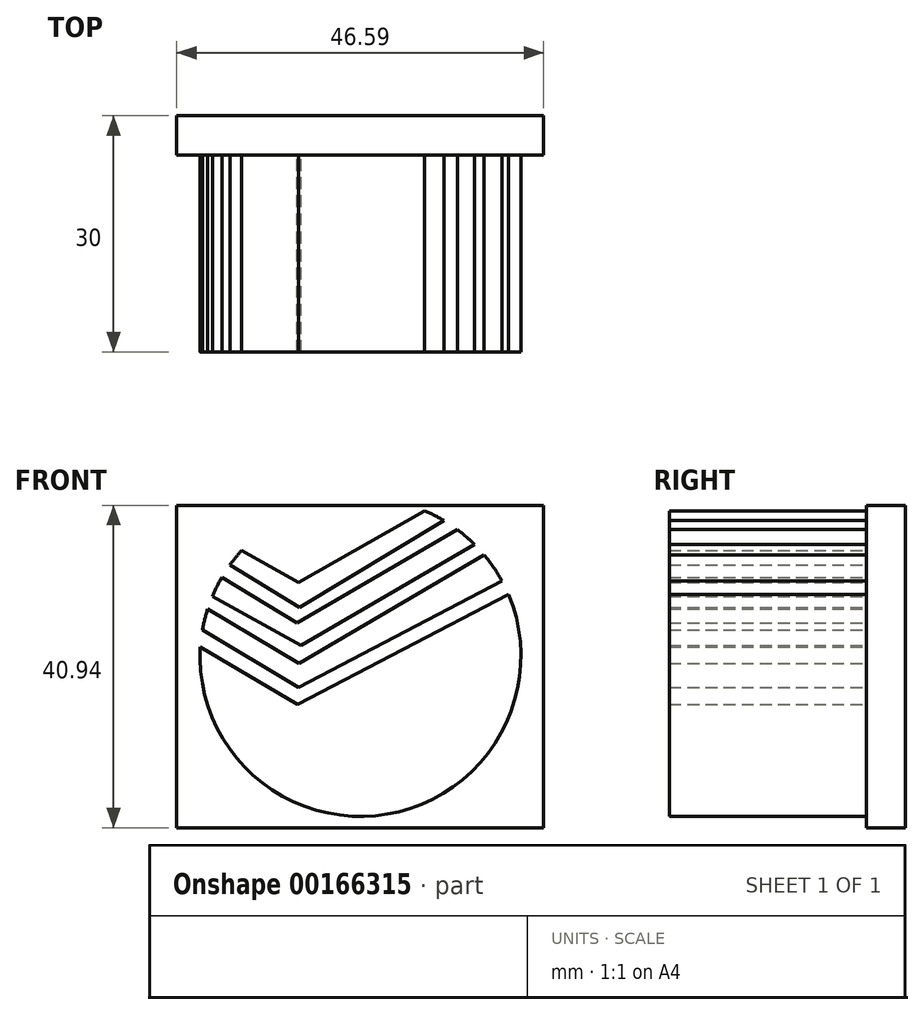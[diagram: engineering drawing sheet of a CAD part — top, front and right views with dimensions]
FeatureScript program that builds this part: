
annotation { "Feature Type Name" : "Feature", "Feature Type Description" : "" }
export const myFeature = defineFeature(function(context is Context, id is Id, definition is map)
    precondition{}
    {
        {
            var Q0;
            Q0=qCreatedBy(makeId("Front.planeOp"),FACE);
            var sketch = newSketch(context, id + "F0", { "sketchPlane" : qUnion([Q0])});
            skLineSegment(sketch, "E0", {"start": v(-23.24, 10.14) * mm, "end": v(-16.04, 6.02) * mm});
            skLineSegment(sketch, "E1", {"start": v(-16.04, 6.02) * mm, "end": v(0, 15.16) * mm});
            skLineSegment(sketch, "E2", {"start": v(-24.76, 8.25) * mm, "end": v(-15.88, 2.88) * mm});
            skLineSegment(sketch, "E3", {"start": v(-15.88, 2.88) * mm, "end": v(2.45, 13.9) * mm});
            skLineSegment(sketch, "E4", {"start": v(-25.77, 6.69) * mm, "end": v(-16.2, 0.9) * mm});
            skLineSegment(sketch, "E5", {"start": v(-16.2, 0.9) * mm, "end": v(4.16, 12.75) * mm});
            skLineSegment(sketch, "E6", {"start": v(-26.97, 4.3) * mm, "end": v(-15.72, -1.97) * mm});
            skLineSegment(sketch, "E7", {"start": v(-15.72, -1.97) * mm, "end": v(6.35, 10.85) * mm});
            skLineSegment(sketch, "E8", {"start": v(-28.24, 0) * mm, "end": v(-16.02, -7.26) * mm});
            skLineSegment(sketch, "E9", {"start": v(-16.02, -7.26) * mm, "end": v(9.84, 6.21) * mm});
            skLineSegment(sketch, "E10", {"start": v(-28.51, -2.13) * mm, "end": v(-16.14, -9.43) * mm});
            skLineSegment(sketch, "E11", {"start": v(-16.14, -9.43) * mm, "end": v(10.66, 4.53) * mm});
            skLineSegment(sketch, "E12", {"start": v(-27.57, 2.66) * mm, "end": v(-15.98, -4.26) * mm});
            skLineSegment(sketch, "E13", {"start": v(-15.98, -4.26) * mm, "end": v(7.54, 9.56) * mm});
            skArc(sketch, "E14", {"start": v(10.66, 4.53) * mm, "mid": v(-11.53, 16.54) * mm, "end": v(-28.51, -2.13) * mm});
            skArc(sketch, "E15", {"start": v(-28.51, -2.13) * mm, "mid": v(-4.74, -23.38) * mm, "end": v(10.66, 4.53) * mm});
            skSolve(sketch);
        }
        {
            var Q0;
            {var subQ2=sQuery(id+"F0.wireOp",EDGE,"E4");Q0=makeQuery(id+"F0.imprint","IMPRINT",FACE,{"disambiguationData":[TD([[makeQuery(id+"F0.imprint","IMPRINT",EDGE,{"derivedFrom":subQ2}),-1.0]])]});}
            var Q1;
            {var subQ4=sQuery(id+"F0.wireOp",EDGE,"E0");Q1=makeQuery(id+"F0.imprint","IMPRINT",FACE,{"disambiguationData":[TD([[makeQuery(id+"F0.imprint","IMPRINT",EDGE,{"derivedFrom":subQ4}),-1.0]])]});}
            var Q2;
            {var subQ3=sQuery(id+"F0.wireOp",EDGE,"E8");Q2=makeQuery(id+"F0.imprint","IMPRINT",FACE,{"disambiguationData":[TD([[makeQuery(id+"F0.imprint","IMPRINT",EDGE,{"derivedFrom":subQ3}),1.0]])]});}
            var Q3;
            Q3=makeQuery(id+"F0.imprint","IMPRINT",FACE,{"disambiguationData":[TD([[makeQuery(id+"F0.imprint","IMPRINT",EDGE,{"derivedFrom":sQuery(id+"F0.wireOp",EDGE,"E10")}),-1.0]])]});
            extrude(context, id + "F1", {"entities" : qUnion([Q0, Q1, Q2, Q3]), "depth" : 25 * mm});
        }
        {
            var Q0;
            Q0=makeQuery(id+"F1.opExtrude","CAP_FACE",FACE,{"disambiguationData":[OSD([sQuery(id+"F0.wireOp",EDGE,"E10"),sQuery(id+"F0.wireOp",EDGE,"E11"),sQuery(id+"F0.wireOp",EDGE,"E15")])],"isStart":true});
            var sketch = newSketch(context, id + "F2", { "sketchPlane" : qUnion([Q0])});
            skLineSegment(sketch, "E16.bottom", {"start": v(-15.08, 15.83) * mm, "end": v(31.51, 15.83) * mm});
            skLineSegment(sketch, "E16.top", {"start": v(-15.08, -25.1) * mm, "end": v(31.51, -25.1) * mm});
            skLineSegment(sketch, "E16.left", {"start": v(-15.08, 15.83) * mm, "end": v(-15.08, -25.1) * mm});
            skLineSegment(sketch, "E16.right", {"start": v(31.51, 15.83) * mm, "end": v(31.51, -25.1) * mm});
            skSolve(sketch);
        }
        {
            var Q0;
            Q0=makeQuery(id+"F2.imprint","IMPRINT",FACE,{"disambiguationData":[TD([[makeQuery(id+"F2.imprint","IMPRINT",EDGE,{"derivedFrom":sQuery(id+"F2.wireOp",EDGE,"E16.bottom")}),-1.0]])]});
            var Q1;
            Q1=makeQuery(id+"F2.imprint","IMPRINT",FACE,{"disambiguationData":[TD([[makeQuery(id+"F2.imprint","IMPRINT",EDGE,{"derivedFrom":makeQuery(id+"F1.opExtrude","CAP_EDGE",EDGE,{"disambiguationData":[OSD([sQuery(id+"F0.wireOp",EDGE,"E10")])],"isStart":true})}),1.0]])]});
            extrude(context, id + "F3", {"entities" : qUnion([Q0, Q1]), "depth" : 5 * mm});
        }
    });
